# Revit family: Strangregulierventil für Differenzdruckmessung, Geradsitzform 4217 GM (LF-MF)
name_source: partatom
category: Rohrzubehör
revit_build: Autodesk Revit 2018 (Build: 20190510_1515(x64)
units: mm (PartAtom-declared; Revit-internal decimal feet)

## family parameters
Arbeitsebenenbasiert = Nein
Beim Laden mit Abzugskörper schneiden = Nein
Bemaßung runder Anschluss = Durchmesser verwenden
Gemeinsam genutzt = Nein
Immer vertikal = Ja
OmniClass-Nummer = 23.65.55.14
OmniClass-Titel = Valves for Liquid Services
Teiletyp = Unterbricht

## types (2) — shared parameters
Anwendungen = Zum hydraulischen Abgleich in Heiz- oder Kühlanlagen, Einregulieren von Verteilleitungen, Strängen, Wärmetauschern, Heiz- und Kühlregistern.
Ausführung = STRÖMAX-GM Strangregulierventil mit Messventilen, 1/2′′ – 3′′
Geradesitzform, gelbe Ausführung, Muffe x Muffe, nichtsteigende Spindel, Spindelabdichtung durch Doppel-O-Ring,Voreinstellung durch Hubbegrenzung mittels Innenspindel, digitale Anzeige der Voreinstellstufe im Handradfenster.
2 Messventile sind neben dem Handrad montiert.
D04 = 9 mm  [stored 0.0295276 ft]
Differenzdruckmessung = STRÖMAX-GM Strangregulierventil ist mit zwei Messventilen ausgestattet.
Bei Verwendung eines geeigneten Messgerätes kann der Differenzdruck gemessen und dadurch die jeweilige Durchflussmenge in Abhängigkeit der Einstellstufe ermittelt werden.
Am HERZ-Messcomputer (1 8900 05) ist außerdem direkt die jeweilige Durchflussmenge ablesbar.
Einbaulage = Bedingt durch die senkrecht zur Ventilachse angeordnete, nichtsteigende Ventilspindel ist für jede Einbaulage optimale Zugängigkeit und Bedienbarkeit des Ventils gewährleistet.
Gehäuse = DZR-Messing
H03 = 10 mm  [stored 0.0328084 ft]
Hersteller = HERZ Armaturen Ges.m.b.H.
MD01 = 9.5 mm  [stored 0.031168 ft]
Max. Betriebsdruck = 1600000.0 Pa
Max. Betriebstemperatur (ab DN40) = 110 °C
Max. Betriebstemperatur (bis DN32) = 130 °C
Medium = Heizwasserqualität entsprechend ÖNORM H 5195 bzw. VDI-Richtlinie 2035.
Die Verwendung von Ethylen- und Propylenglykol ist im Mischungsverhältnis 25 - 50 Vol. % zulässig.
S02 = 60 mm  [stored 0.19685 ft]
SCRNCODE = 05;07;02
SCRNSEQ = ARM;ARM_TYP="STRV";2
URL = www.herz-armaturen.at
W01 = 30.00°
W02 = 60.00°
zero-valued in all types: SC_NennweiteBerechnet

## type names (no varying parameters)
- LF
- MF

note: [stored X ft] marks values corroborated as IEEE doubles in the binary element streams (Revit-internal decimal feet)
